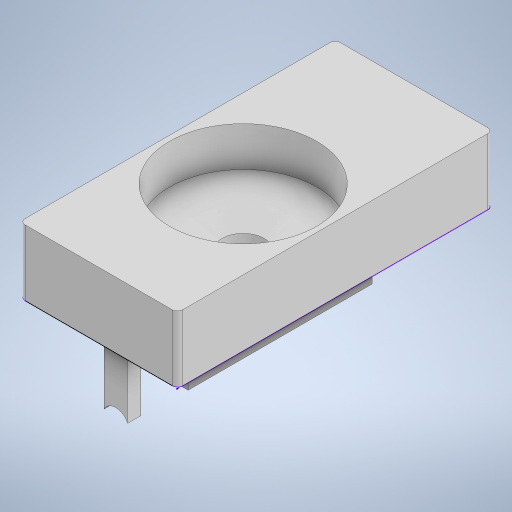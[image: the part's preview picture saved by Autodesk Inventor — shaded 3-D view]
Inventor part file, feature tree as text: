
AUTODESK INVENTOR PART (.ipt)
format: ipt  version: 2023 (Build 270158000, 158)  size: 830,976 bytes
history: native  units: in
note: dims shown in document units (in); Inventor stores cm internally (conversion verified against a paired STEP export)
features: sketch x17, extrude x16, plane x8, projected_geometry x5, revolve x1, fillet x1
ambient origin geometry x8: Origin, YZ Plane, XZ Plane, XY Plane, X Axis, Y Axis, Z Axis, Center Point
bodies: Solid1 (feature_tree)
feature tree (48):
  sketch  "Sketch1"  dims[d0=2.3622in d1=4.7244in]
  extrude  "Extrusion1"  Depth=4.7244in
  plane  "Work Plane1"
  sketch  "Sketch2"  dims[d2=1.7717in d3=0.1969in]
  plane  "Work Plane2"
  extrude  "Extrusion2"  Depth=0.1969in
  extrude  "Extrusion3"  TaperAngle=0.0deg  [1 undecoded]
  plane  "Work Plane6"
  sketch  "Sketch3"  dims[d4=0.9843in d5=0.0in]
  sketch  "Sketch4"  dims[d6=0.4921in d7=0.3937in]
  sketch  "Sketch5"  dims[d8=0.0984in d9=0.8858in]
  extrude  "Extrusion4"  Depth=0.3937in
  extrude  "Extrusion5"  Depth=0.8858in
  extrude  "Extrusion6"  Depth=0.9843in
  extrude  "Extrusion7"  Depth=0.8268in
  plane  "Work Plane7"
  revolve  "Revolution2"  [1 undecoded]
  extrude  "Extrusion8"  Depth=0.3937in
  fillet  "Fillet1"  [1 undecoded]
  extrude  "Extrusion9"  [1 undecoded]
  sketch  "Sketch11"  dims[d20=90.0deg d21=-1.378in]
  sketch  "Sketch13"  dims[d22=1.7717in d23=0.7874in d24=0.0in]
  plane  "Work Plane8"
  sketch  "Sketch14"  dims[d25=2.3622in d26=2.3622in]
  extrude  "Extrusion12"  Depth=0.7874in TaperAngle=0.0deg
  extrude  "Extrusion14"  Depth=2.3622in
  extrude  "Extrusion15"  Depth=1.1811in
  extrude  "Extrusion16"  TaperAngle=0.0deg  [1 undecoded]
  extrude  "Extrusion17"  Depth=0.3937in TaperAngle=0.0deg
  extrude  "Extrusion18"  Depth=0.1969in TaperAngle=0.0deg
  extrude  "Extrusion19"  Depth=0.315in
  projected_geometry  "Projected Loop1"
  plane  "Work Plane3"
  plane  "Work Plane4"
  plane  "Work Plane5"
  sketch  "Sketch7"  dims[d10=-2.7559in d11=0.9843in]
  projected_geometry  "Projected Loop2"
  sketch  "Sketch8"  dims[d12=90.0deg d13=0.8268in]
  projected_geometry  "Projected Loop3"
  projected_geometry  "Projected Loop4"
  sketch  "Sketch9"  dims[d14=0.1969in d15=0.3937in]
  sketch  "Sketch10"  dims[d16=90.0deg d17=0.3937in d19=-2.7559in]
  sketch  "Sketch16"  dims[d27=1.1811in d28=1.1811in]
  sketch  "Sketch20"  dims[d29=0.3937in d30=0.0in d31=0.0in d32=0.0in]
  sketch  "Sketch22"  dims[d33=0.3937in d34=0.0in d35=0.3937in d36=0.0in]
  sketch  "Sketch23"  dims[d37=0.3937in d38=0.0in d40=0.1969in d41=0.0in]
  projected_geometry  "Projected Loop10"
  sketch  "Sketch24"  dims[d42=-1.1811in d43=0.315in d44=0.315in d46=0.1181in d47=360.0deg d48=2.2047in d49=0.1969in d50=0.0in d51=0.0787in d52=0.0in d53=0.0in d54=0.0197in d55=0.0197in d56=0.0197in d57=0.0197in d58=0.0197in d59=0.0197in d73=0.0197in d74=0.0394in d75=1.378in d76=0.0in d82=1.1811in d83=0.0in d95=1.1811in d96=0.0in d102=0.0197in d103=0.0197in d104=0.0197in d105=0.0197in d106=0.0197in d107=1.1811in d108=0.0in d109=0.0in d110=0.0in d111=0.0in d112=0.0in d116=0.3937in d117=0.1969in d118=0.0in d119=0.0in d120=0.0197in d121=0.0197in d122=0.0197in d123=0.0197in d124=0.3937in d125=1.1811in d126=1.811in d39=0.0in d113=0.0197in d114=0.0344in d115=0.0197in]
note: 5 required parameter values undecoded (feature->parameter linkage not recoverable at this tier; creation-order binding heuristic only, values carry confidence <= 0.55)